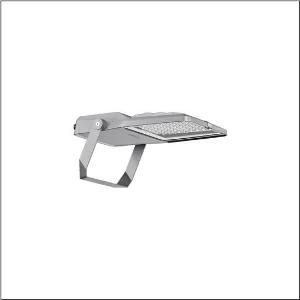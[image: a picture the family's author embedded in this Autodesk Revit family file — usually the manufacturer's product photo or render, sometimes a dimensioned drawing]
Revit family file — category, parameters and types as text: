
# Revit family: floodlight_fl_21_iq_mini___rs12_5xa7772d1b1a_349d
name_source: partatom
category: Lighting Fixtures
units: mm (PartAtom-declared; Revit-internal decimal feet)

## family parameters
Cut with Voids When Loaded = No
Host = Face
Light Source = No
Part Type = Normal
Room Calculation Point = No
Round Connector Dimension = Use Diameter
Shared = No

## types (1)
- --- (1 x LED, 14920 lm, 143 W, 2200K)
    Apparent Load = 143 VA
    CIE Flux Codes = 79 92 99 100 100
    Color Rendering = 70
    Color Temperature = 2200K
    Default Elevation = 1800 mm
    Description = Floodlight FL 21 iQ mini, floodlight, primary light control with lens, of PMMA, primary optical cover: protective disc, of toughened safety glass, transparent, light distribution: RS12, light emission: direct distribution, installation type: surface-mounted, LED, High Power LED, rated luminous flux: 14.920lm, luminous efficacy: 104lm/W, light colour: 722, colour temperature: 2200K, control: Street-Remote, Auto-Match, Temp-Guard, Night-Set, Smart-Wire, Desk-Remote (wireless, voltage-free reading and setting of iQ features in the workshop via application-optimized NFC function/RFID function), optimised constant luminous flux control (CLO 2.0), with terminal, 6-pole, mains connection: 220..240V, AC, 50/60Hz, start of lifetime: 143W, end of service life: 152W, reduction: 61W, luminaire housing, of diecast aluminium, powder-coated, Siteco® metallic grey (DB 702S), corrosivity category C5 mid according to DIN EN ISO 12944, sealing non-destructively replaceable, mounting bracket, of steel, galvanised, powder-coated, Siteco® metallic grey (DB 702S), protection rating (complete): IP66, insulation class (complete): insulation class II (safety insulation), certification: CE, ENEC, VDE, protection symbol: D, impact resistance: IK08, permissible operating ambient temperature: -40..+40°C, permissible operating ambient temperature for outdoor applications: -40..+50°C, standard: DIN EN 12944, LABS conformity tested according to VDMA 24364:2018-05, packaging unit: 1 piece

Light Distribution: RS12
    Height = 70 mm
    Lamp = 1 x LED
    Lamp Light Flux = 14920 lm
    Lamp Power = 143 W
    Lamp count = 1
    Length = 485 mm
    Luminous efficacy = 104 lm/W
    Manufacturer = Siteco
    ModVariant = No
    Model = 5XA7772D1B1A
    Number of Poles = 1
    OnlyDefault = Yes
    Power Factor = 1
    Product Name = Floodlight FL 21 iQ mini | RS12
    Product group = floodlight | pylon annexe
    ProductGroupID = 6200
    Protection Class = Protection class II
    Protection Degree = IP 66
    RLX_Detail_Level = 1
    RLX_Emergency_Light_Flux = 0 lm
    RLX_Emergency_Type = 0
    RLX_Emergency_Type_DB = No
    RlxData = <blob elided: 91213 chars, md5=efa6d7a6>
    Socket = socket
    Standby Power = 0 W
    System Light Flux = 14920 lm
    System Power = 143 W
    Type Comments = factory setting: luminous flux: 100 % | dim-lin: 254 | 730 mA
    Type Image = l_1006845.jpg
    URL = http://relux.com
    VarID = @adj_117581
    Voltage = 0 V
    Weight = 0.00 kg
    Width = 337 mm

## geometry (parser evidence)
native form markers: Blend x4, Sweep x14
no freeform markers — native parametric forms only
